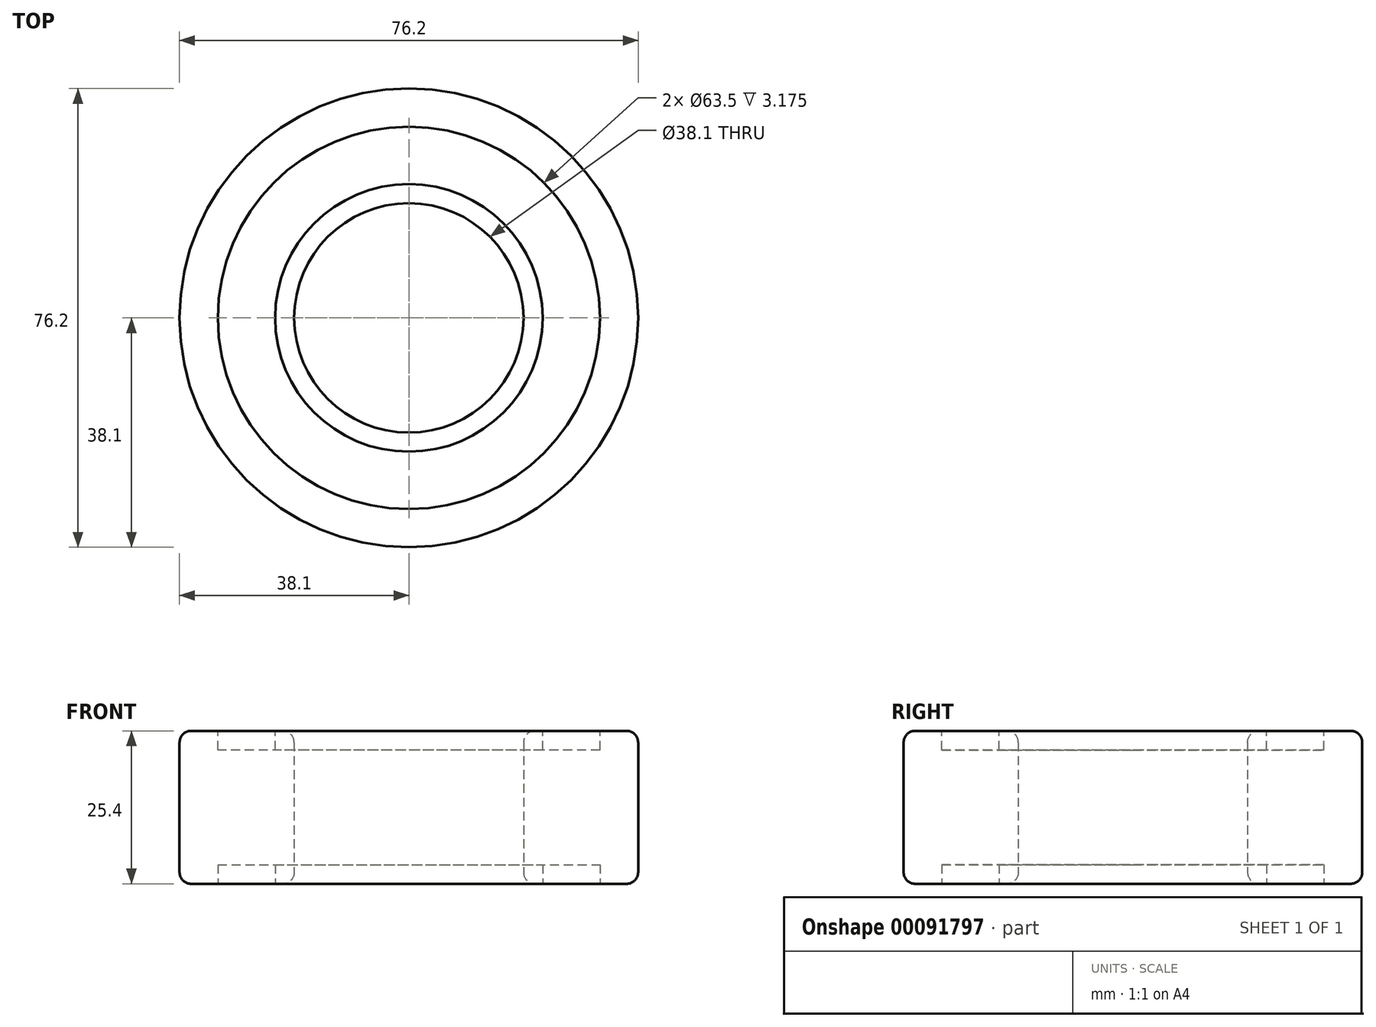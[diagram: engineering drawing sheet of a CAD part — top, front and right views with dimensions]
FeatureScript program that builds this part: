
annotation { "Feature Type Name" : "Feature", "Feature Type Description" : "" }
export const myFeature = defineFeature(function(context is Context, id is Id, definition is map)
    precondition{}
    {
        {
            var Q0;
            Q0=qCreatedBy(makeId("Top.planeOp"),FACE);
            var sketch = newSketch(context, id + "F0", { "sketchPlane" : qUnion([Q0])});
            skCircle(sketch, "E0", {"center": v(0, 0) * mm, "radius": 38.1 * mm});
            skCircle(sketch, "E1", {"center": v(0, 0) * mm, "radius": 19.05 * mm});
            skSolve(sketch);
        }
        {
            var Q0;
            Q0 = qSketchRegion(id + "F0", true);
            extrude(context, id + "F1", {"entities" : qUnion([Q0]), "depth" : 25.4 * mm});
        }
        {
            var Q0;
            Q0=makeQuery(id+"F1.opExtrude","CAP_FACE",FACE,{"disambiguationData":[OSD([sQuery(id+"F0.wireOp",EDGE,"E0"),sQuery(id+"F0.wireOp",EDGE,"E1")])],"isStart":false});
            var sketch = newSketch(context, id + "F2", { "sketchPlane" : qUnion([Q0])});
            skCircle(sketch, "E2", {"center": v(0, 0) * mm, "radius": 22.23 * mm});
            skCircle(sketch, "E3", {"center": v(0, 0) * mm, "radius": 31.75 * mm});
            skSolve(sketch);
        }
        {
            var Q0;
            Q0 = qSketchRegion(id + "F2", true);
            extrude(context, id + "F3", {"entities" : qUnion([Q0]), "operationType" : NewBodyOperationType.REMOVE, "oppositeDirection" : true, "depth" : 3.17 * mm});
        }
        {
            var Q0;
            Q0=makeQuery(id+"F1.opExtrude","CAP_FACE",FACE,{"disambiguationData":[OSD([sQuery(id+"F0.wireOp",EDGE,"E0"),sQuery(id+"F0.wireOp",EDGE,"E1")])],"isStart":true});
            var sketch = newSketch(context, id + "F4", { "sketchPlane" : qUnion([Q0])});
            skCircle(sketch, "E4", {"center": v(0, 0) * mm, "radius": 22.23 * mm});
            skCircle(sketch, "E5", {"center": v(0, 0) * mm, "radius": 31.75 * mm});
            skSolve(sketch);
        }
        {
            var Q0;
            Q0 = qSketchRegion(id + "F4", true);
            extrude(context, id + "F5", {"entities" : qUnion([Q0]), "operationType" : NewBodyOperationType.REMOVE, "oppositeDirection" : true, "depth" : 3.17 * mm});
        }
        {
            var Q0;
            Q0=makeQuery(id+"F1.opExtrude","CAP_EDGE",EDGE,{"disambiguationData":[OSD([sQuery(id+"F0.wireOp",EDGE,"E0")])],"isStart":true});
            var Q1;
            Q1=makeQuery(id+"F1.opExtrude","CAP_EDGE",EDGE,{"disambiguationData":[OSD([sQuery(id+"F0.wireOp",EDGE,"E0")])],"isStart":false});
            var Q2;
            Q2=makeQuery(id+"F1.opExtrude","CAP_EDGE",EDGE,{"disambiguationData":[OSD([sQuery(id+"F0.wireOp",EDGE,"E1")])],"isStart":true});
            var Q3;
            Q3=makeQuery(id+"F1.opExtrude","CAP_EDGE",EDGE,{"disambiguationData":[OSD([sQuery(id+"F0.wireOp",EDGE,"E1")])],"isStart":false});
            fillet(context, id + "F6", {"entities" : qUnion([Q0, Q1, Q2, Q3]), "radius" : 1.9 * mm, "tangentPropagation" : true, "allowEdgeOverflow" : false});
        }
    });
